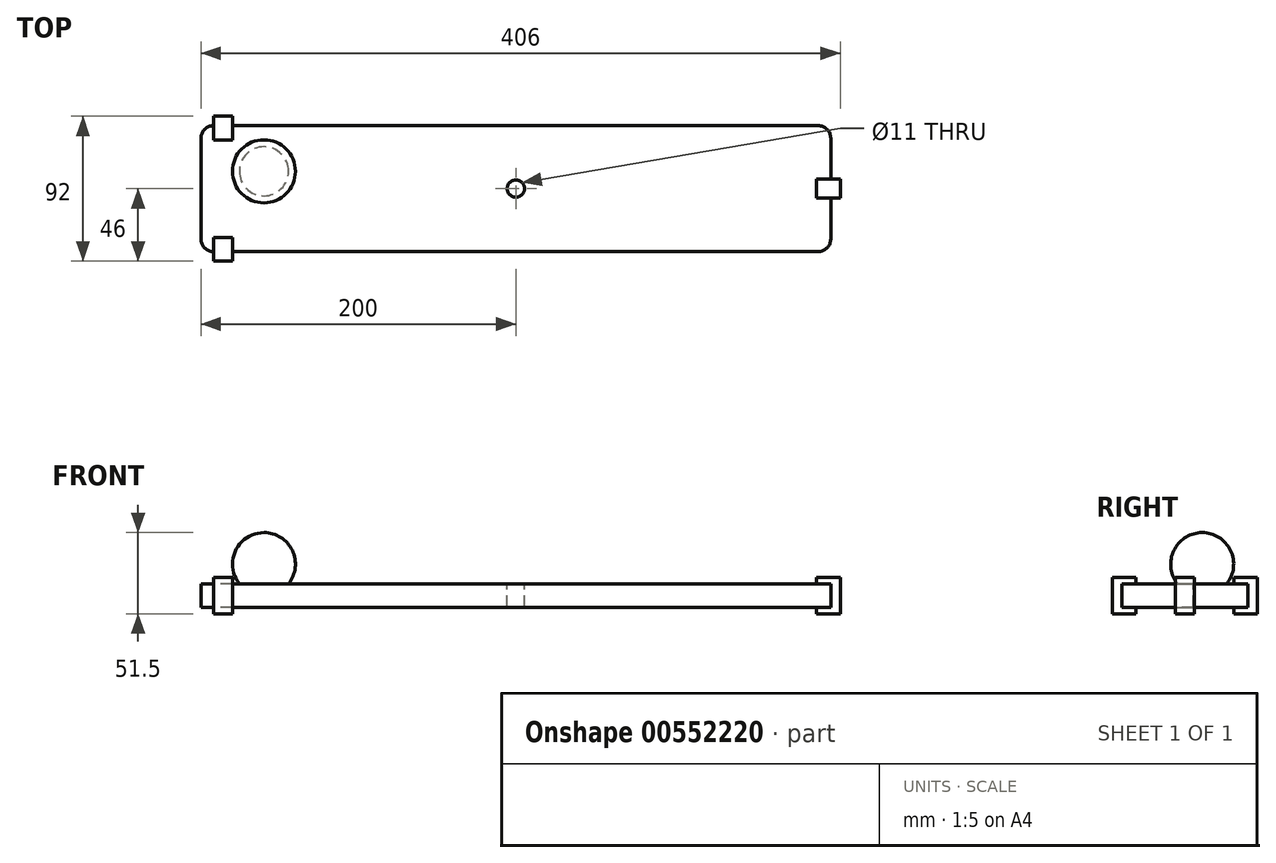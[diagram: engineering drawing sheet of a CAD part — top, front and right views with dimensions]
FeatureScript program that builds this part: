
annotation { "Feature Type Name" : "Feature", "Feature Type Description" : "" }
export const myFeature = defineFeature(function(context is Context, id is Id, definition is map)
    precondition{}
    {
        {
            var Q0;
            Q0=qCreatedBy(makeId("Top.planeOp"),FACE);
            var sketch = newSketch(context, id + "F0", { "sketchPlane" : qUnion([Q0])});
            skLineSegment(sketch, "E0.bottom", {"start": v(200, -40) * mm, "end": v(-200, -40) * mm});
            skLineSegment(sketch, "E0.top", {"start": v(200, 40) * mm, "end": v(-200, 40) * mm});
            skLineSegment(sketch, "E0.left", {"start": v(200, -40) * mm, "end": v(200, 40) * mm});
            skLineSegment(sketch, "E0.right", {"start": v(-200, -40) * mm, "end": v(-200, 40) * mm});
            skPoint(sketch, "E0.middle", {"position": v(0, 0) * mm});
            skSolve(sketch);
        }
        {
            var Q0;
            Q0 = qSketchRegion(id + "F0", true);
            extrude(context, id + "F1", {"entities" : qUnion([Q0]), "endBound" : BoundingType.SYMMETRIC, "depth" : 15 * mm, "offsetDistance" : 25 * mm});
        }
        {
            var Q0;
            Q0=makeQuery(id+"F1.opExtrude","SWEPT_EDGE",EDGE,{"disambiguationData":[OSD([sQuery(id+"F0.wireOp",EDGE,"E0.bottom"),sQuery(id+"F0.wireOp",EDGE,"E0.right")])]});
            var Q1;
            Q1=makeQuery(id+"F1.opExtrude","SWEPT_EDGE",EDGE,{"disambiguationData":[OSD([sQuery(id+"F0.wireOp",EDGE,"E0.bottom"),sQuery(id+"F0.wireOp",EDGE,"E0.left")])]});
            var Q2;
            Q2=makeQuery(id+"F1.opExtrude","SWEPT_EDGE",EDGE,{"disambiguationData":[OSD([sQuery(id+"F0.wireOp",EDGE,"E0.top"),sQuery(id+"F0.wireOp",EDGE,"E0.left")])]});
            var Q3;
            Q3=makeQuery(id+"F1.opExtrude","SWEPT_EDGE",EDGE,{"disambiguationData":[OSD([sQuery(id+"F0.wireOp",EDGE,"E0.top"),sQuery(id+"F0.wireOp",EDGE,"E0.right")])]});
            fillet(context, id + "F2", {"entities" : qUnion([Q0, Q1, Q2, Q3]), "radius" : 8 * mm, "tangentPropagation" : true, "allowEdgeOverflow" : false});
        }
        {
            var Q0;
            Q0=qCreatedBy(makeId("Top.planeOp"),FACE);
            var sketch = newSketch(context, id + "F3", { "sketchPlane" : qUnion([Q0])});
            skLineSegment(sketch, "E1.bottom", {"start": v(-200, -40) * mm, "end": v(-192, -40) * mm, "construction": true});
            skLineSegment(sketch, "E1.top", {"start": v(-200, -31) * mm, "end": v(-192, -31) * mm, "construction": true});
            skLineSegment(sketch, "E1.left", {"start": v(-200, -40) * mm, "end": v(-200, -31) * mm, "construction": true});
            skLineSegment(sketch, "E1.right", {"start": v(-192, -40) * mm, "end": v(-192, -31) * mm, "construction": true});
            skLineSegment(sketch, "E2.bottom", {"start": v(-192, -31) * mm, "end": v(-180, -31) * mm});
            skLineSegment(sketch, "E2.top", {"start": v(-192, -46) * mm, "end": v(-180, -46) * mm});
            skLineSegment(sketch, "E2.left", {"start": v(-192, -31) * mm, "end": v(-192, -46) * mm});
            skLineSegment(sketch, "E2.right", {"start": v(-180, -31) * mm, "end": v(-180, -46) * mm});
            skLineSegment(sketch, "E3.bottom", {"start": v(-200, 40) * mm, "end": v(-192, 40) * mm, "construction": true});
            skLineSegment(sketch, "E3.top", {"start": v(-200, 31) * mm, "end": v(-192, 31) * mm, "construction": true});
            skLineSegment(sketch, "E3.left", {"start": v(-200, 40) * mm, "end": v(-200, 31) * mm, "construction": true});
            skLineSegment(sketch, "E3.right", {"start": v(-192, 40) * mm, "end": v(-192, 31) * mm, "construction": true});
            skLineSegment(sketch, "E4.bottom", {"start": v(-192, 31) * mm, "end": v(-180, 31) * mm});
            skLineSegment(sketch, "E4.top", {"start": v(-192, 46) * mm, "end": v(-180, 46) * mm});
            skLineSegment(sketch, "E4.left", {"start": v(-192, 31) * mm, "end": v(-192, 46) * mm});
            skLineSegment(sketch, "E4.right", {"start": v(-180, 31) * mm, "end": v(-180, 46) * mm});
            skLineSegment(sketch, "E5", {"start": v(200, 40) * mm, "end": v(200, 0) * mm, "construction": true});
            skLineSegment(sketch, "E6", {"start": v(200, 0) * mm, "end": v(200, -40) * mm, "construction": true});
            skLineSegment(sketch, "E7", {"start": v(200, 0) * mm, "end": v(191, 0) * mm, "construction": true});
            skLineSegment(sketch, "E8.bottom", {"start": v(191, 6) * mm, "end": v(206, 6) * mm});
            skLineSegment(sketch, "E8.top", {"start": v(191, -6) * mm, "end": v(206, -6) * mm});
            skLineSegment(sketch, "E8.left", {"start": v(191, 6) * mm, "end": v(191, -6) * mm});
            skLineSegment(sketch, "E8.right", {"start": v(206, 6) * mm, "end": v(206, -6) * mm});
            skSolve(sketch);
        }
        {
            var Q0;
            Q0 = qSketchRegion(id + "F3", true);
            extrude(context, id + "F4", {"entities" : qUnion([Q0]), "operationType" : NewBodyOperationType.ADD, "endBound" : BoundingType.SYMMETRIC, "depth" : 23 * mm, "offsetDistance" : 25 * mm});
        }
        {
            var Q0;
            Q0=makeQuery(id+"F1.opExtrude","CAP_FACE",FACE,{"disambiguationData":[OSD([sQuery(id+"F0.wireOp",EDGE,"E0.bottom"),sQuery(id+"F0.wireOp",EDGE,"E0.top"),sQuery(id+"F0.wireOp",EDGE,"E0.left"),sQuery(id+"F0.wireOp",EDGE,"E0.right")])],"isStart":false});
            var sketch = newSketch(context, id + "F5", { "sketchPlane" : qUnion([Q0])});
            skCircle(sketch, "E9", {"center": v(0, 0) * mm, "radius": 5.5 * mm});
            skSolve(sketch);
        }
        {
            var Q0;
            Q0 = qSketchRegion(id + "F5", true);
            extrude(context, id + "F6", {"entities" : qUnion([Q0]), "operationType" : NewBodyOperationType.REMOVE, "oppositeDirection" : true, "depth" : 25 * mm, "offsetDistance" : 25 * mm});
        }
        {
            var Q0;
            Q0=qCreatedBy(makeId("Top.planeOp"),FACE);
            var sketch = newSketch(context, id + "F7", { "sketchPlane" : qUnion([Q0])});
            skLineSegment(sketch, "E10.bottom", {"start": v(-180, 31) * mm, "end": v(-140, 31) * mm, "construction": true});
            skLineSegment(sketch, "E10.top", {"start": v(-180, -9) * mm, "end": v(-140, -9) * mm, "construction": true});
            skLineSegment(sketch, "E10.left", {"start": v(-180, 31) * mm, "end": v(-180, -9) * mm, "construction": true});
            skLineSegment(sketch, "E10.right", {"start": v(-140, 31) * mm, "end": v(-140, -9) * mm, "construction": true});
            skLineSegment(sketch, "E11", {"start": v(-180, 31) * mm, "end": v(-140, -9) * mm, "construction": true});
            skPoint(sketch, "E12", {"position": v(-160, 11) * mm});
            skSolve(sketch);
        }
        {
            var Q0;
            Q0=sQuery(id+"F7.wireOp",EDGE,"E11");
            cPoint(context, id + "F8", {"entities" : qUnion([Q0]), "parameter" : 0.5});
        }
        {
            var Q0;
            Q0 = qCreatedBy(id + "F8" ,VERTEX);
            var Q1;
            Q1=qCreatedBy(makeId("Front.planeOp"),FACE);
            cPlane(context, id + "F9", {"entities" : qUnion([Q0, Q1]), "cplaneType" : CPlaneType.PLANE_POINT, "offset" : 25 * mm, "width" : 150 * mm, "height" : 150 * mm});
        }
        {
            var Q0;
            Q0=qCreatedBy(id+"F9.planeOp",FACE);
            var sketch = newSketch(context, id + "F10", { "sketchPlane" : qUnion([Q0])});
            skLineSegment(sketch, "E13", {"start": v(-160, 0) * mm, "end": v(-160, 20) * mm, "construction": true});
            skArc(sketch, "E14", {"start": v(-160, 0) * mm, "mid": v(-140, 20) * mm, "end": v(-160, 40) * mm});
            skLineSegment(sketch, "E15", {"start": v(-160, 0) * mm, "end": v(-160, 40) * mm});
            skSolve(sketch);
        }
        {
            var Q0;
            Q0 = qSketchRegion(id + "F10", true);
            var Q1;
            Q1=sQuery(id+"F10.wireOp",EDGE,"E15");
            revolve(context, id + "F11", {"operationType" : NewBodyOperationType.ADD, "entities" : qUnion([Q0]), "axis" : qUnion([Q1]), "revolveType" : RevolveType.FULL});
        }
    });
